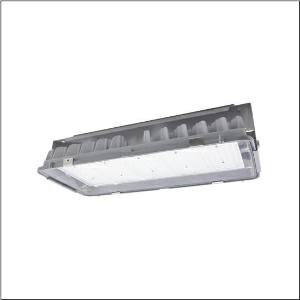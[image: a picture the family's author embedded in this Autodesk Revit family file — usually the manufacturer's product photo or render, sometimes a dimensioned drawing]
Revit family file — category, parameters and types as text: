
# Revit family: highbay_11xtreme_51hf82da4nma
name_source: partatom
category: Lighting Fixtures
units: mm (PartAtom-declared; Revit-internal decimal feet)

## family parameters
Cut with Voids When Loaded = No
Host = Face
Light Source = No
Part Type = Normal
Room Calculation Point = No
Round Connector Dimension = Use Diameter
Shared = No

## types (1)
- --- (1 x LED, 33700 lm, 187.7 W, 4000K)
    Apparent Load = 188 VA
    CIE Flux Codes = 84 96 100 100 100
    Color Rendering = 80
    Color Temperature = 4000K
    Default Elevation = 1800 mm
    Description = Highbay 11Xtreme, LED high bay luminaire, primary light control with lens, of PMMA, primary optical cover: cover, of toughened safety glass, light emission: direct distribution, primary light characteristic: symmetric, installation type: suspended mounting, surface-mounted, 1x LED module,for 1x LED, rated luminous flux: 33.700lm, luminous efficacy: 180lm/W, light colour: 840, colour temperature: 4000K, with cable H07RN-F 5x 1.5mm², mains connection: 220..240V, AC, 50/60Hz, cable length: 1,5m, rated input power: 188W, luminaire housing, of diecast aluminium, partly coated, silver, length: 595mm, width: 280mm, height: 195mm, protection rating (complete): IP66, insulation class (complete): insulation class I (protective earthing), certification: CE, ENEC, UKCA, protection symbol: D, ball protection: ball impact resistant according to DIN VDE 0710 part 13 (with chain suspension), impact resistance: IK08, permissible operating ambient temperature: -25..+45°C, reducing of maximum allowable ambient temperature of 5°C with ceiling mounting, packaging unit: 1 piece
    Height = 157 mm
    Lamp = 1 x LED
    Lamp Light Flux = 33700 lm
    Lamp Power = 187.7 W
    Lamp count = 1
    Length = 593 mm
    Luminous efficacy = 180 lm/W
    Manufacturer = Siteco
    ModVariant = No
    Model = 51HF82DA4NMA
    Mounting Place = Ceiling
    Mounting Type = Pendant
    Number of Poles = 1
    OnlyDefault = Yes
    Power Factor = 1
    Product Name = Highbay 11Xtreme
    Product group = LED high bay luminaire
    ProductGroupID = 903
    Protection Class = Protection class I
    Protection Degree = IP 66
    RLX_Detail_Level = 1
    RLX_Emergency_Light_Flux = 0 lm
    RLX_Emergency_Type = 0
    RLX_Emergency_Type_DB = No
    RlxData = <blob elided: 28357 chars, md5=04c37ee4>
    Socket = socket
    Standby Power = 0 W
    System Light Flux = 33700 lm
    System Power = 188 W
    Type Comments = factory setting: luminous flux: 100 % | dim-lin: 254 | 1255 mA
    Type Image = l_1258342.jpg
    URL = http://relux.com
    VarID = @adj_035545
    Voltage = 0 V
    Weight = 0.00 kg
    Width = 568 mm

## geometry (parser evidence)
native form markers: Blend x4, Sweep x10
no freeform markers — native parametric forms only
